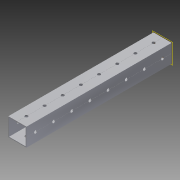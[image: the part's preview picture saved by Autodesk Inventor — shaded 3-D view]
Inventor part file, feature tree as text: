
AUTODESK INVENTOR PART (.ipt)
format: ipt  version: 2014 (Build 180170000, 170)  size: 1,157,632 bytes
history: native  units: in
note: dims shown in document units (in); Inventor stores cm internally (conversion verified against a paired STEP export)
features: pattern_circular x1, other x1, plane x1, extrude x1, imported_body x1, sketch x1
ambient origin geometry x8: Origin, YZ Plane, XZ Plane, XY Plane, X Axis, Y Axis, Z Axis, Center Point
bodies: Body1 (feature_tree)
feature tree (6):
  pattern_circular  "CirPattern2"
  other  "217-3426-STEP1"
  plane  "Work Plane1"
  extrude  "Extrusion1"  Depth=3937.0079in TaperAngle=0.0deg
  imported_body  "Base1"
  sketch  "Sketch1"  dims[d0=-6.0in d1=3937.0079in d2=0.0in]
